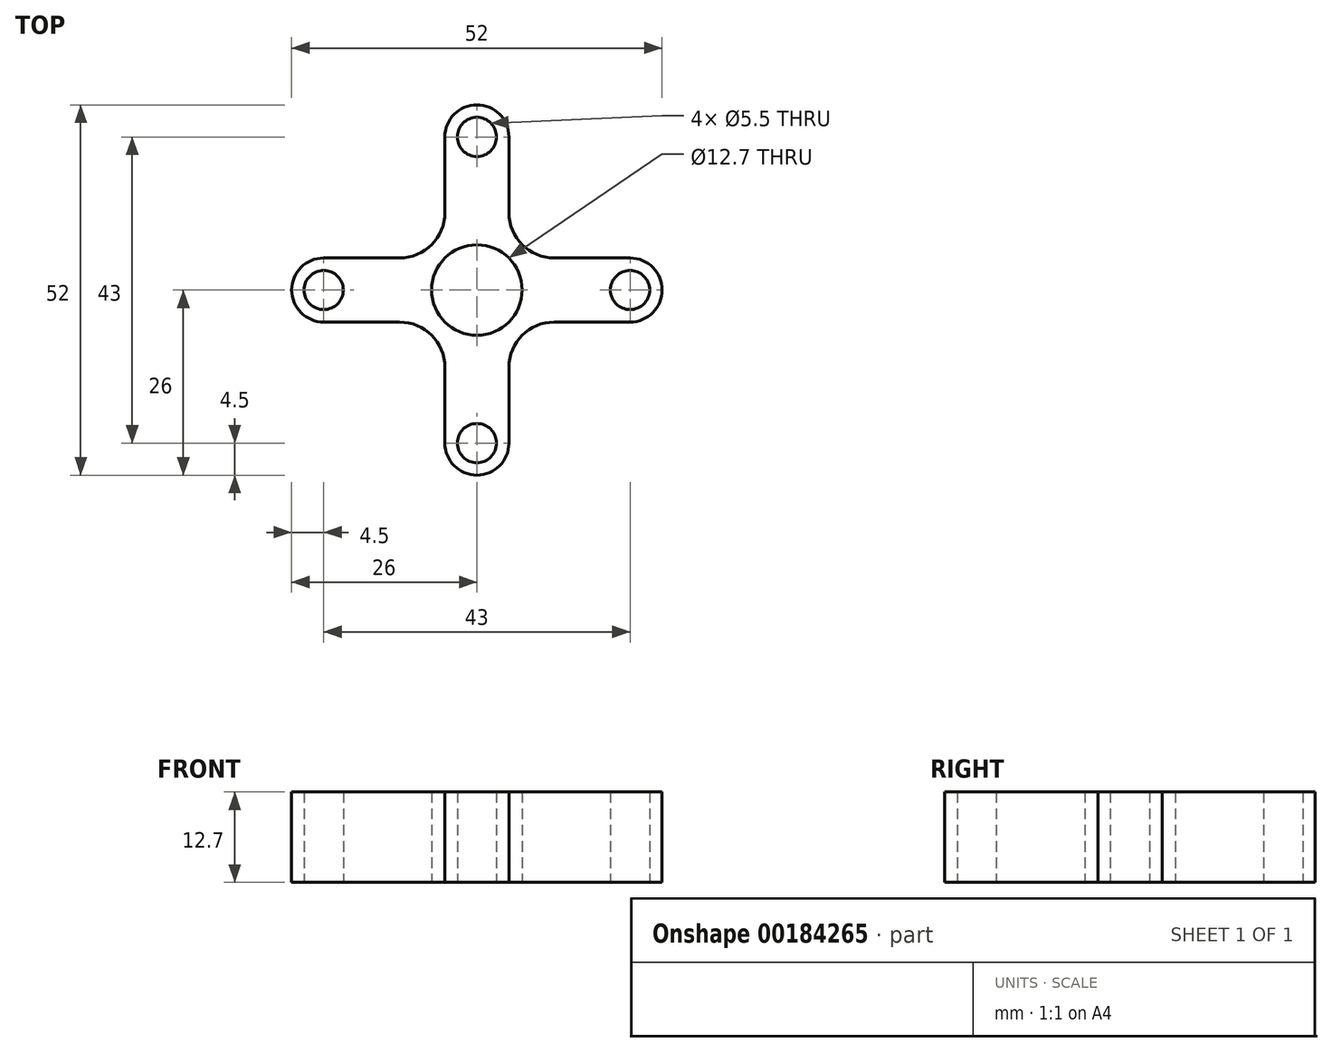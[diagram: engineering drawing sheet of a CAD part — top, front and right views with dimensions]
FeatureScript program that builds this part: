
annotation { "Feature Type Name" : "Feature", "Feature Type Description" : "" }
export const myFeature = defineFeature(function(context is Context, id is Id, definition is map)
    precondition{}
    {
        {
            var Q0;
            Q0=qCreatedBy(makeId("Top.planeOp"),FACE);
            var sketch = newSketch(context, id + "F0", { "sketchPlane" : qUnion([Q0])});
            skCircle(sketch, "E0", {"center": v(0, 21.5) * mm, "radius": 2.75 * mm});
            skCircle(sketch, "E1.1.0", {"center": v(-21.5, 0) * mm, "radius": 2.75 * mm});
            skCircle(sketch, "E1.2.0", {"center": v(0, -21.5) * mm, "radius": 2.75 * mm});
            skCircle(sketch, "E1.3.0", {"center": v(21.5, 0) * mm, "radius": 2.75 * mm});
            skPoint(sketch, "E1.center", {"position": v(0, 0) * mm});
            skCircle(sketch, "E2", {"center": v(0, 0) * mm, "radius": 6.35 * mm});
            skArc(sketch, "E3", {"start": v(4.5, 21.5) * mm, "mid": v(0, 26) * mm, "end": v(-4.5, 21.5) * mm});
            skArc(sketch, "E4.1.0", {"start": v(-21.5, 4.5) * mm, "mid": v(-26, 0) * mm, "end": v(-21.5, -4.5) * mm});
            skArc(sketch, "E4.2.0", {"start": v(-4.5, -21.5) * mm, "mid": v(0, -26) * mm, "end": v(4.5, -21.5) * mm});
            skArc(sketch, "E4.3.0", {"start": v(21.5, -4.5) * mm, "mid": v(26, 0) * mm, "end": v(21.5, 4.5) * mm});
            skLineSegment(sketch, "E5", {"start": v(-21.5, 4.5) * mm, "end": v(-10.85, 4.5) * mm});
            skLineSegment(sketch, "E6", {"start": v(-4.5, 21.5) * mm, "end": v(-4.5, 10.85) * mm});
            skPoint(sketch, "E7.newPointA", {"position": v(-3.91, 4.5) * mm});
            skPoint(sketch, "E7.newPointB", {"position": v(-4.5, 4.5) * mm});
            skArc(sketch, "E7.filletArc", {"start": v(-10.85, 4.5) * mm, "mid": v(-6.36, 6.36) * mm, "end": v(-4.5, 10.85) * mm});
            skLineSegment(sketch, "E8.MirrorCS", {"start": v(4.5, 21.5) * mm, "end": v(4.5, 10.85) * mm});
            skLineSegment(sketch, "E9.MirrorCS", {"start": v(21.5, 4.5) * mm, "end": v(10.85, 4.5) * mm});
            skArc(sketch, "E10.MirrorCS", {"start": v(10.85, 4.5) * mm, "mid": v(6.36, 6.36) * mm, "end": v(4.5, 10.85) * mm});
            skLineSegment(sketch, "E11.MirrorCS", {"start": v(-21.5, -4.5) * mm, "end": v(-10.85, -4.5) * mm});
            skArc(sketch, "E12.MirrorCS", {"start": v(-10.85, -4.5) * mm, "mid": v(-6.36, -6.36) * mm, "end": v(-4.5, -10.85) * mm});
            skLineSegment(sketch, "E13.MirrorCS", {"start": v(-4.5, -21.5) * mm, "end": v(-4.5, -10.85) * mm});
            skLineSegment(sketch, "E14.MirrorCS", {"start": v(21.5, -4.5) * mm, "end": v(10.85, -4.5) * mm});
            skLineSegment(sketch, "E15.MirrorCS", {"start": v(4.5, -21.5) * mm, "end": v(4.5, -10.85) * mm});
            skArc(sketch, "E16.MirrorCS", {"start": v(10.85, -4.5) * mm, "mid": v(6.36, -6.36) * mm, "end": v(4.5, -10.85) * mm});
            skSolve(sketch);
        }
        {
            var Q0;
            Q0 = qSketchRegion(id + "F0", true);
            extrude(context, id + "F1", {"entities" : qUnion([Q0]), "depth" : 12.7 * mm});
        }
    });
